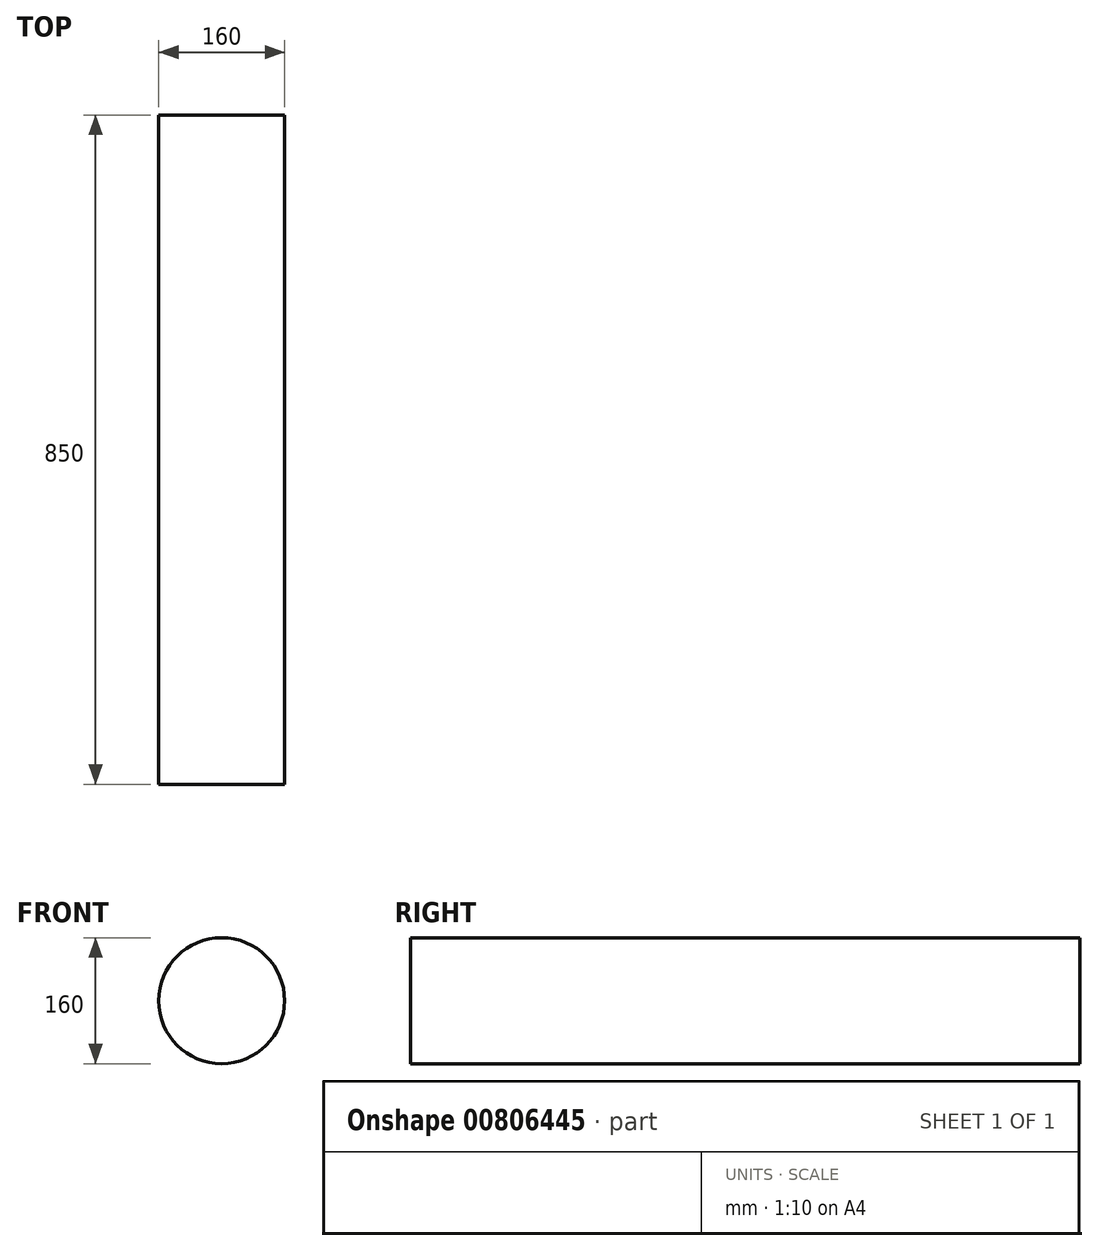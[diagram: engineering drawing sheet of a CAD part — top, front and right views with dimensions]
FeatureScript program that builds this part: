
annotation { "Feature Type Name" : "Feature", "Feature Type Description" : "" }
export const myFeature = defineFeature(function(context is Context, id is Id, definition is map)
    precondition{}
    {
        {
            var Q0;
            Q0=qCreatedBy(makeId("Front.planeOp"),FACE);
            var sketch = newSketch(context, id + "F0", { "sketchPlane" : qUnion([Q0])});
            skCircle(sketch, "E0", {"center": v(0, 0) * mm, "radius": 80 * mm});
            skSolve(sketch);
        }
        {
            var Q0;
            Q0=makeQuery(id+"F0.imprint","IMPRINT",FACE,{"disambiguationData":[TD([[makeQuery(id+"F0.imprint","IMPRINT",EDGE,{"derivedFrom":sQuery(id+"F0.wireOp",EDGE,"E0")}),1.0]])]});
            extrude(context, id + "F1", {"entities" : qUnion([Q0]), "depth" : 850 * mm, "offsetDistance" : 25 * mm});
        }
    });
